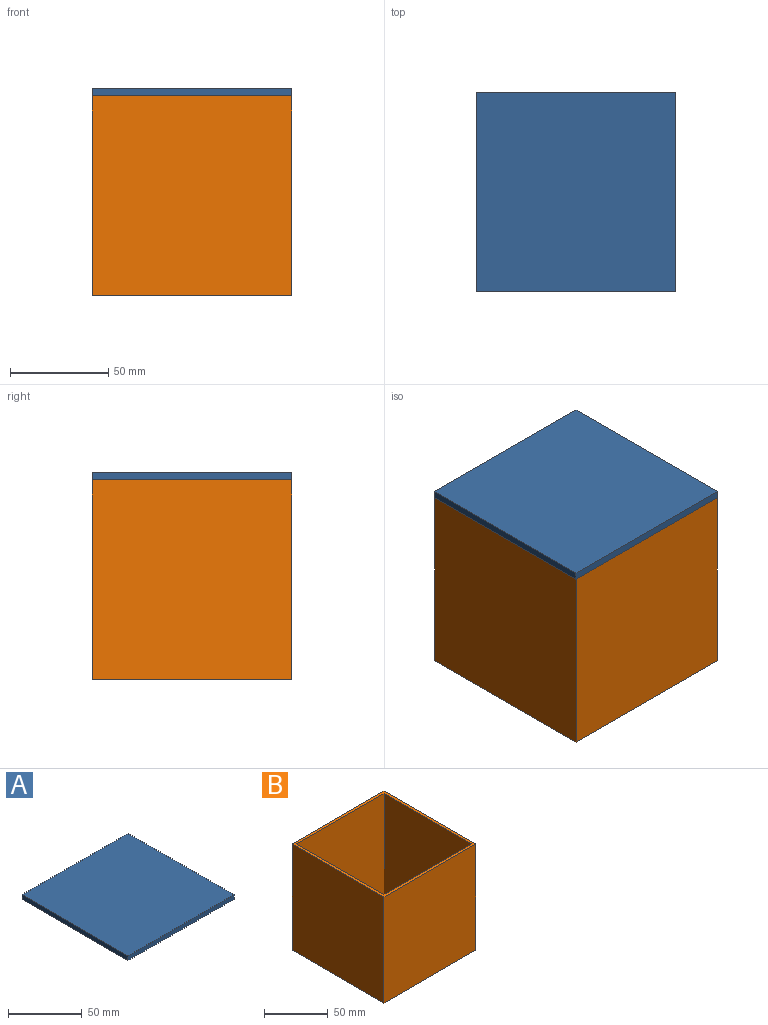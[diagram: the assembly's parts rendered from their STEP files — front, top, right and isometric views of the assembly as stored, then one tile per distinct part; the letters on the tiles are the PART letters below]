
ASSEMBLY  parts=2 mates=1
PART A: 6 faces, bbox 101.6x101.6x3.8 mm
  f0: plane 101.6x3.81mm, normal (1,0,0), area 387.1mm2, adj f1,f3,f4,f5
  f1: plane 101.6x3.81mm, normal (0,1,0), area 387.1mm2, adj f0,f2,f4,f5
  f2: plane 101.6x3.81mm, normal (-1,0,0), area 387.1mm2, adj f1,f3,f4,f5
  f3: plane 101.6x3.81mm, normal (0,-1,0), area 387.1mm2, adj f0,f2,f4,f5
  f4: plane 101.6x101.6mm, normal (0,0,1), area 10322.6mm2, adj f0,f1,f2,f3
  f5: plane 101.6x101.6mm, normal (0,0,-1), area 10322.6mm2, adj f0,f1,f2,f3
PART B: 11 faces, bbox 101.6x101.6x101.6 mm
  f0: plane 101.6x101.6mm, normal (0,0,1), area 1006.4mm2, adj f1,f2,f3,f4,f6,f7,f8,f9
  f1: plane 101.6x101.6mm, normal (1,0,0), area 10322.6mm2, adj f0,f2,f4,f5
  f2: plane 101.6x101.6mm, normal (0,1,0), area 10322.6mm2, adj f0,f1,f3,f5
  f3: plane 101.6x101.6mm, normal (-1,0,0), area 10322.6mm2, adj f0,f2,f4,f5
  f4: plane 101.6x101.6mm, normal (0,-1,0), area 10322.6mm2, adj f0,f1,f3,f5
  f5: plane 101.6x101.6mm, normal (0,0,-1), area 10322.6mm2, adj f1,f2,f3,f4
  f6: plane 99.06x96.52mm, normal (-1,0,0), area 9561.3mm2, adj f0,f7,f9,f10
  f7: plane 99.06x96.52mm, normal (0,-1,0), area 9561.3mm2, adj f0,f6,f8,f10
  f8: plane 99.06x96.52mm, normal (1,0,0), area 9561.3mm2, adj f0,f7,f9,f10
  f9: plane 99.06x96.52mm, normal (0,1,0), area 9561.3mm2, adj f0,f6,f8,f10
  f10: plane 96.52x96.52mm, normal (0,0,1), area 9316.1mm2, adj f6,f7,f8,f9
PLACE A t=(-10.86,-14.77,58.2)mm
PLACE B t=(-10.67,-5.08,7.4)mm
MATE fastened B.f0 <-> A.f5  axis (0,0,1) through (-61.66,-65.57,58.2)mm
